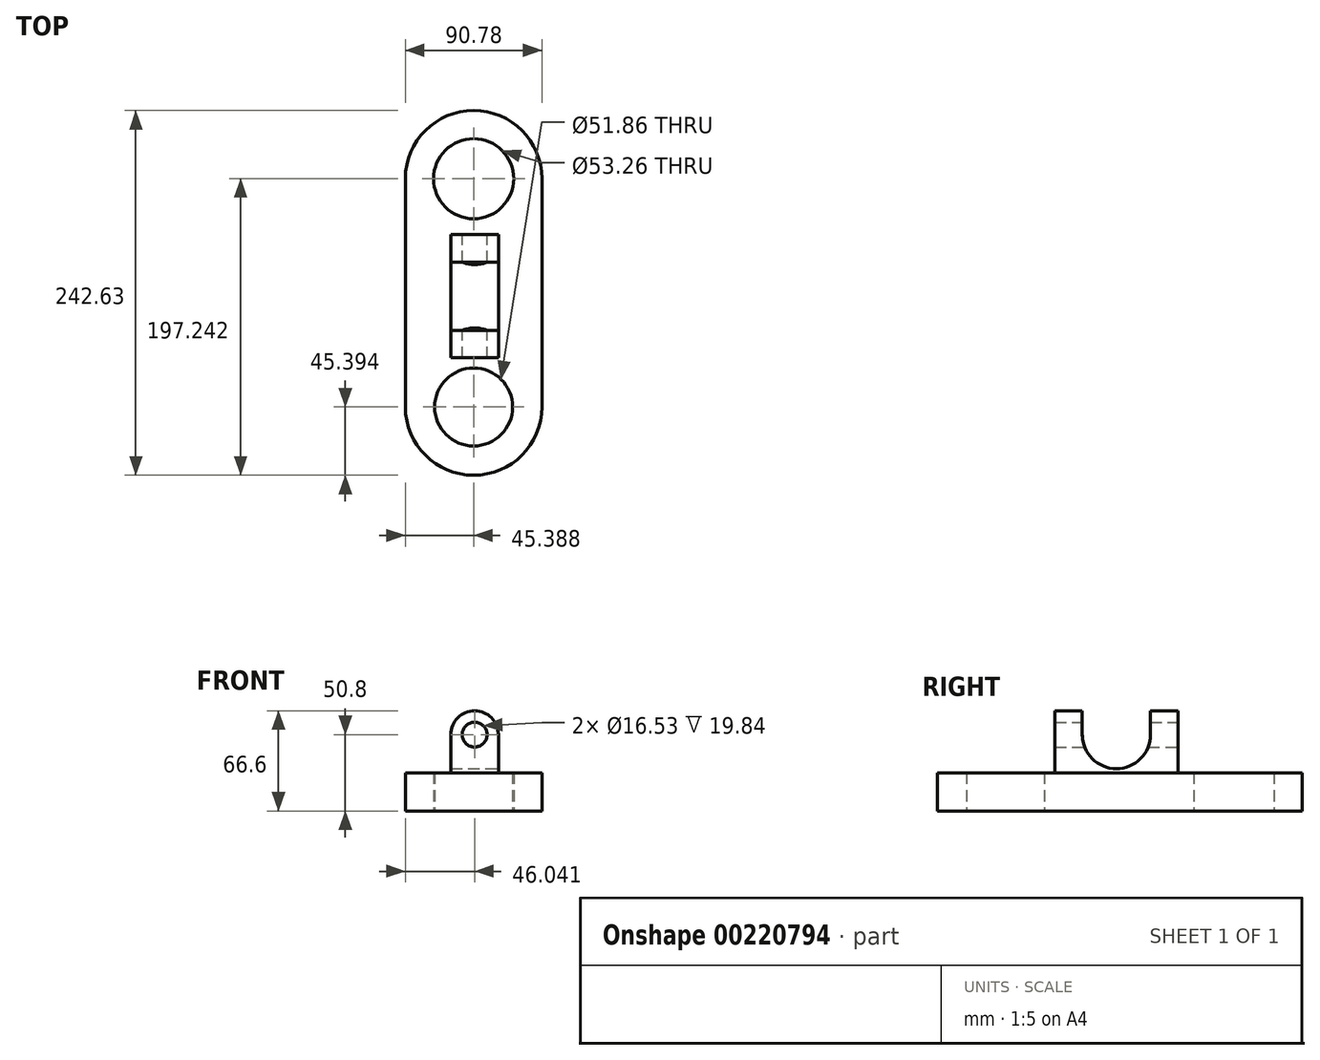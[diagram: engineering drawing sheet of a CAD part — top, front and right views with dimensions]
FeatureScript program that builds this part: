
annotation { "Feature Type Name" : "Feature", "Feature Type Description" : "" }
export const myFeature = defineFeature(function(context is Context, id is Id, definition is map)
    precondition{}
    {
        {
            var Q0;
            Q0=qCreatedBy(makeId("Top.planeOp"),FACE);
            var sketch = newSketch(context, id + "F0", { "sketchPlane" : qUnion([Q0])});
            skLineSegment(sketch, "E0.bottom", {"start": v(-45.64, 75.71) * mm, "end": v(45.14, 75.71) * mm});
            skLineSegment(sketch, "E0.top", {"start": v(-45.64, -76.14) * mm, "end": v(45.14, -76.14) * mm});
            skLineSegment(sketch, "E0.left", {"start": v(-45.64, 75.71) * mm, "end": v(-45.64, -76.14) * mm});
            skLineSegment(sketch, "E0.right", {"start": v(45.14, 75.71) * mm, "end": v(45.14, -76.14) * mm});
            skArc(sketch, "E1", {"start": v(45.14, 75.71) * mm, "mid": v(-0.25, 121.1) * mm, "end": v(-45.64, 75.71) * mm});
            skArc(sketch, "E2", {"start": v(-45.64, -76.14) * mm, "mid": v(-0.25, -121.53) * mm, "end": v(45.14, -76.14) * mm});
            skCircle(sketch, "E3", {"center": v(-0.25, 75.71) * mm, "radius": 26.63 * mm});
            skCircle(sketch, "E4", {"center": v(-0.25, -76.14) * mm, "radius": 25.93 * mm});
            skSolve(sketch);
        }
        {
            var Q0;
            {var subQ6=sQuery(id+"F0.wireOp",EDGE,"E0.left");Q0=makeQuery(id+"F0.imprint","IMPRINT",FACE,{"disambiguationData":[TD([[makeQuery(id+"F0.imprint","IMPRINT",EDGE,{"derivedFrom":subQ6}),1.0]])]});}
            var Q1;
            {var subQ0=sQuery(id+"F0.wireOp",EDGE,"E1");Q1=makeQuery(id+"F0.imprint","IMPRINT",FACE,{"disambiguationData":[TD([[makeQuery(id+"F0.imprint","IMPRINT",EDGE,{"derivedFrom":subQ0}),1.0]])]});}
            var Q2;
            {var subQ0=sQuery(id+"F0.wireOp",EDGE,"E2");Q2=makeQuery(id+"F0.imprint","IMPRINT",FACE,{"disambiguationData":[TD([[makeQuery(id+"F0.imprint","IMPRINT",EDGE,{"derivedFrom":subQ0}),1.0]])]});}
            extrude(context, id + "F1", {"entities" : qUnion([Q0, Q1, Q2]), "depth" : 25.4 * mm});
        }
        {
            var Q0;
            Q0=qCreatedBy(makeId("Top.planeOp"),FACE);
            var sketch = newSketch(context, id + "F2", { "sketchPlane" : qUnion([Q0])});
            skLineSegment(sketch, "E5.bottom", {"start": v(16.2, 38.46) * mm, "end": v(-15.4, 38.46) * mm});
            skLineSegment(sketch, "E5.top", {"start": v(16.2, -43.42) * mm, "end": v(-15.4, -43.42) * mm});
            skLineSegment(sketch, "E5.left", {"start": v(16.2, 38.46) * mm, "end": v(16.2, -43.42) * mm});
            skLineSegment(sketch, "E5.right", {"start": v(-15.4, 38.46) * mm, "end": v(-15.4, -43.42) * mm});
            skSolve(sketch);
        }
        {
            var Q0;
            Q0=makeQuery(id+"F2.imprint","IMPRINT",FACE,{"disambiguationData":[TD([[makeQuery(id+"F2.imprint","IMPRINT",EDGE,{"derivedFrom":sQuery(id+"F2.wireOp",EDGE,"E5.bottom")}),1.0]])]});
            extrude(context, id + "F3", {"entities" : qUnion([Q0]), "operationType" : NewBodyOperationType.ADD, "depth" : 50.8 * mm});
        }
        {
            var Q0;
            Q0=makeQuery(id+"F3.opExtrude","SWEPT_FACE",FACE,{"disambiguationData":[OSD([sQuery(id+"F2.wireOp",EDGE,"E5.left")])]});
            var sketch = newSketch(context, id + "F4", { "sketchPlane" : qUnion([Q0])});
            skCircle(sketch, "E6", {"center": v(-2.48, 50.8) * mm, "radius": 22.66 * mm});
            skSolve(sketch);
        }
        {
            var Q0;
            {var subQ0=sQuery(id+"F4.wireOp",EDGE,"E6");var subQ1=makeQuery(id+"F3.opExtrude","CAP_EDGE",EDGE,{"disambiguationData":[OSD([sQuery(id+"F2.wireOp",EDGE,"E5.left")])],"isStart":false});var subQ2=makeQuery(id+"F4.imprint","INTERSECT",VERTEX,{"disambiguationData":[OD(0.0)],"derivedFrom":[subQ1,subQ0]});Q0=makeQuery(id+"F4.imprint","IMPRINT",FACE,{"disambiguationData":[TD([[makeQuery(id+"F4.imprint","IMPRINT",EDGE,{"disambiguationData":[TD([[subQ2,-1.0]])],"derivedFrom":subQ0}),1.0]])]});}
            var Q1;
            {var subQ0=sQuery(id+"F4.wireOp",EDGE,"E6");var subQ1=makeQuery(id+"F3.opExtrude","CAP_EDGE",EDGE,{"disambiguationData":[OSD([sQuery(id+"F2.wireOp",EDGE,"E5.left")])],"isStart":false});var subQ2=makeQuery(id+"F4.imprint","INTERSECT",VERTEX,{"disambiguationData":[OD(0.0)],"derivedFrom":[subQ1,subQ0]});Q1=makeQuery(id+"F4.imprint","IMPRINT",FACE,{"disambiguationData":[TD([[makeQuery(id+"F4.imprint","IMPRINT",EDGE,{"disambiguationData":[TD([[subQ2,1.0]])],"derivedFrom":subQ0}),1.0]])]});}
            extrude(context, id + "F5", {"entities" : qUnion([Q0, Q1]), "operationType" : NewBodyOperationType.REMOVE, "oppositeDirection" : true, "depth" : 76.2 * mm});
        }
        {
            var Q0;
            {var subQ0=sQuery(id+"F2.wireOp",EDGE,"E5.top");var subQ1=sQuery(id+"F2.wireOp",EDGE,"E5.left");var subQ2=sQuery(id+"F2.wireOp",EDGE,"E5.right");Q0=makeQuery(id+"F5.boolean.opBoolean","SPLIT",FACE,{"disambiguationData":[TD([makeQuery(id+"F3.opExtrude","SWEPT_FACE",FACE,{"disambiguationData":[OSD([subQ0])]})])],"derivedFrom":makeQuery(id+"F3.opExtrude","CAP_FACE",FACE,{"disambiguationData":[OSD([sQuery(id+"F2.wireOp",EDGE,"E5.bottom"),subQ0,subQ1,subQ2])],"isStart":false})});}
            var sketch = newSketch(context, id + "F6", { "sketchPlane" : qUnion([Q0])});
            skLineSegment(sketch, "E7.bottom", {"start": v(-15.4, -25.14) * mm, "end": v(0.4, -25.14) * mm});
            skLineSegment(sketch, "E7.top", {"start": v(-15.4, -43.42) * mm, "end": v(0.4, -43.42) * mm});
            skLineSegment(sketch, "E7.left", {"start": v(-15.4, -25.14) * mm, "end": v(-15.4, -43.42) * mm});
            skLineSegment(sketch, "E7.right", {"start": v(0.4, -25.14) * mm, "end": v(0.4, -43.42) * mm});
            skSolve(sketch);
        }
        {
            var Q0;
            Q0=makeQuery(id+"F6.imprint","IMPRINT",FACE,{"disambiguationData":[TD([[makeQuery(id+"F6.imprint","IMPRINT",EDGE,{"derivedFrom":sQuery(id+"F6.wireOp",EDGE,"E7.bottom")}),-1.0]])]});
            var Q1;
            Q1=sQuery(id+"F6.wireOp",EDGE,"E7.right");
            revolve(context, id + "F7", {"operationType" : NewBodyOperationType.ADD, "entities" : qUnion([Q0]), "axis" : qUnion([Q1]), "revolveType" : RevolveType.FULL});
        }
        {
            var Q0;
            {var subQ0=sQuery(id+"F2.wireOp",EDGE,"E5.bottom");var subQ1=sQuery(id+"F2.wireOp",EDGE,"E5.left");var subQ2=sQuery(id+"F2.wireOp",EDGE,"E5.right");Q0=makeQuery(id+"F5.boolean.opBoolean","SPLIT",FACE,{"disambiguationData":[TD([makeQuery(id+"F3.opExtrude","SWEPT_FACE",FACE,{"disambiguationData":[OSD([subQ0])]})])],"derivedFrom":makeQuery(id+"F3.opExtrude","CAP_FACE",FACE,{"disambiguationData":[OSD([subQ0,sQuery(id+"F2.wireOp",EDGE,"E5.top"),subQ1,subQ2])],"isStart":false})});}
            var sketch = newSketch(context, id + "F8", { "sketchPlane" : qUnion([Q0])});
            skLineSegment(sketch, "E8.bottom", {"start": v(-15.4, 38.46) * mm, "end": v(0.4, 38.46) * mm});
            skLineSegment(sketch, "E8.top", {"start": v(-15.4, 20.19) * mm, "end": v(0.4, 20.19) * mm});
            skLineSegment(sketch, "E8.left", {"start": v(-15.4, 38.46) * mm, "end": v(-15.4, 20.19) * mm});
            skLineSegment(sketch, "E8.right", {"start": v(0.4, 38.46) * mm, "end": v(0.4, 20.19) * mm});
            skSolve(sketch);
        }
        {
            var Q0;
            Q0=makeQuery(id+"F8.imprint","IMPRINT",FACE,{"disambiguationData":[TD([[makeQuery(id+"F8.imprint","IMPRINT",EDGE,{"derivedFrom":sQuery(id+"F8.wireOp",EDGE,"E8.bottom")}),1.0]])]});
            var Q1;
            Q1=sQuery(id+"F8.wireOp",EDGE,"E8.right");
            revolve(context, id + "F9", {"operationType" : NewBodyOperationType.ADD, "entities" : qUnion([Q0]), "axis" : qUnion([Q1]), "revolveType" : RevolveType.FULL});
        }
        {
            var Q0;
            Q0=makeQuery(id+"F9.boolean.opBoolean","MERGE",FACE,{"derivedFrom":[makeQuery(id+"F3.opExtrude","SWEPT_FACE",FACE,{"disambiguationData":[OSD([sQuery(id+"F2.wireOp",EDGE,"E5.bottom")])]}),makeQuery(id+"F9.opRevolve","SWEPT_FACE",FACE,{"disambiguationData":[OSD([sQuery(id+"F8.wireOp",EDGE,"E8.bottom")])]})]});
            var sketch = newSketch(context, id + "F10", { "sketchPlane" : qUnion([Q0])});
            skCircle(sketch, "E9", {"center": v(-0.4, 50.8) * mm, "radius": 8.26 * mm});
            skSolve(sketch);
        }
        {
            var Q0;
            Q0=makeQuery(id+"F10.imprint","IMPRINT",FACE,{"disambiguationData":[TD([[makeQuery(id+"F10.imprint","IMPRINT",EDGE,{"derivedFrom":sQuery(id+"F10.wireOp",EDGE,"E9")}),1.0]])]});
            extrude(context, id + "F11", {"entities" : qUnion([Q0]), "operationType" : NewBodyOperationType.REMOVE, "oppositeDirection" : true, "depth" : 135.64 * mm});
        }
    });
